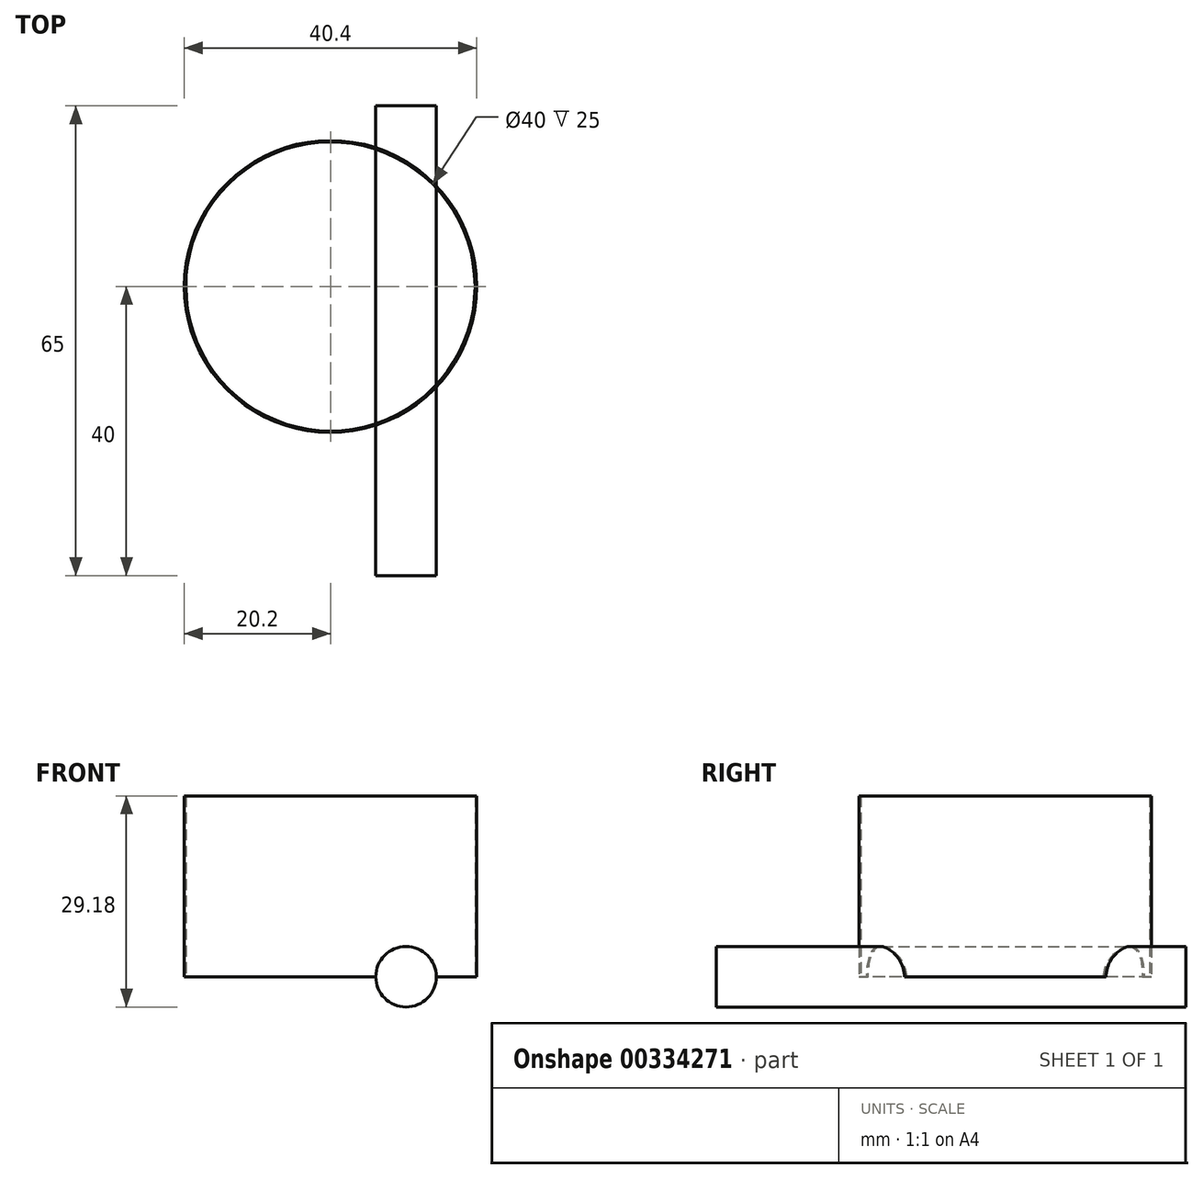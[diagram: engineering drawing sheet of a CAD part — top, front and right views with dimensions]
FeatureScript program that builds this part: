
annotation { "Feature Type Name" : "Feature", "Feature Type Description" : "" }
export const myFeature = defineFeature(function(context is Context, id is Id, definition is map)
    precondition{}
    {
        {
            var Q0;
            Q0=qCreatedBy(makeId("Top.planeOp"),FACE);
            var sketch = newSketch(context, id + "F0", { "sketchPlane" : qUnion([Q0])});
            skCircle(sketch, "E0", {"center": v(0, 0) * mm, "radius": 20.2 * mm});
            skSolve(sketch);
        }
        {
            var Q0;
            Q0=qCreatedBy(makeId("Top.planeOp"),FACE);
            var sketch = newSketch(context, id + "F1", { "sketchPlane" : qUnion([Q0])});
            skCircle(sketch, "E1", {"center": v(0, 0) * mm, "radius": 20 * mm});
            skSolve(sketch);
        }
        {
            var Q0;
            Q0 = qSketchRegion(id + "F0", true);
            extrude(context, id + "F2", {"entities" : qUnion([Q0]), "depth" : 25 * mm});
        }
        {
            var Q0;
            Q0 = qSketchRegion(id + "F1", true);
            extrude(context, id + "F3", {"entities" : qUnion([Q0]), "operationType" : NewBodyOperationType.REMOVE, "endBound" : BoundingType.SYMMETRIC, "depth" : 25 * mm});
        }
        {
            var Q0;
            Q0=makeQuery(id+"F3.boolean.opBoolean","COPY",FACE,{"derivedFrom":makeQuery(id+"F3.opExtrude","CAP_FACE",FACE,{"disambiguationData":[OSD([sQuery(id+"F1.wireOp",EDGE,"E1")])],"isStart":false})});
            extrude(context, id + "F4", {"entities" : qUnion([Q0]), "operationType" : NewBodyOperationType.REMOVE, "oppositeDirection" : true, "depth" : 25 * mm});
        }
        {
            var Q0;
            Q0=qCreatedBy(makeId("Front.planeOp"),FACE);
            var sketch = newSketch(context, id + "F5", { "sketchPlane" : qUnion([Q0])});
            skCircle(sketch, "E2", {"center": v(10.45, 0) * mm, "radius": 4.18 * mm});
            skSolve(sketch);
        }
        {
            var Q0;
            Q0 = qSketchRegion(id + "F5", true);
            extrude(context, id + "F6", {"entities" : qUnion([Q0]), "operationType" : NewBodyOperationType.ADD, "depth" : 40 * mm});
        }
        {
            var Q0;
            Q0=makeQuery(id+"F6.opExtrude","CAP_FACE",FACE,{"disambiguationData":[OSD([sQuery(id+"F5.wireOp",EDGE,"E2")])],"isStart":true});
            extrude(context, id + "F7", {"entities" : qUnion([Q0]), "operationType" : NewBodyOperationType.ADD, "depth" : 25 * mm});
        }
    });
